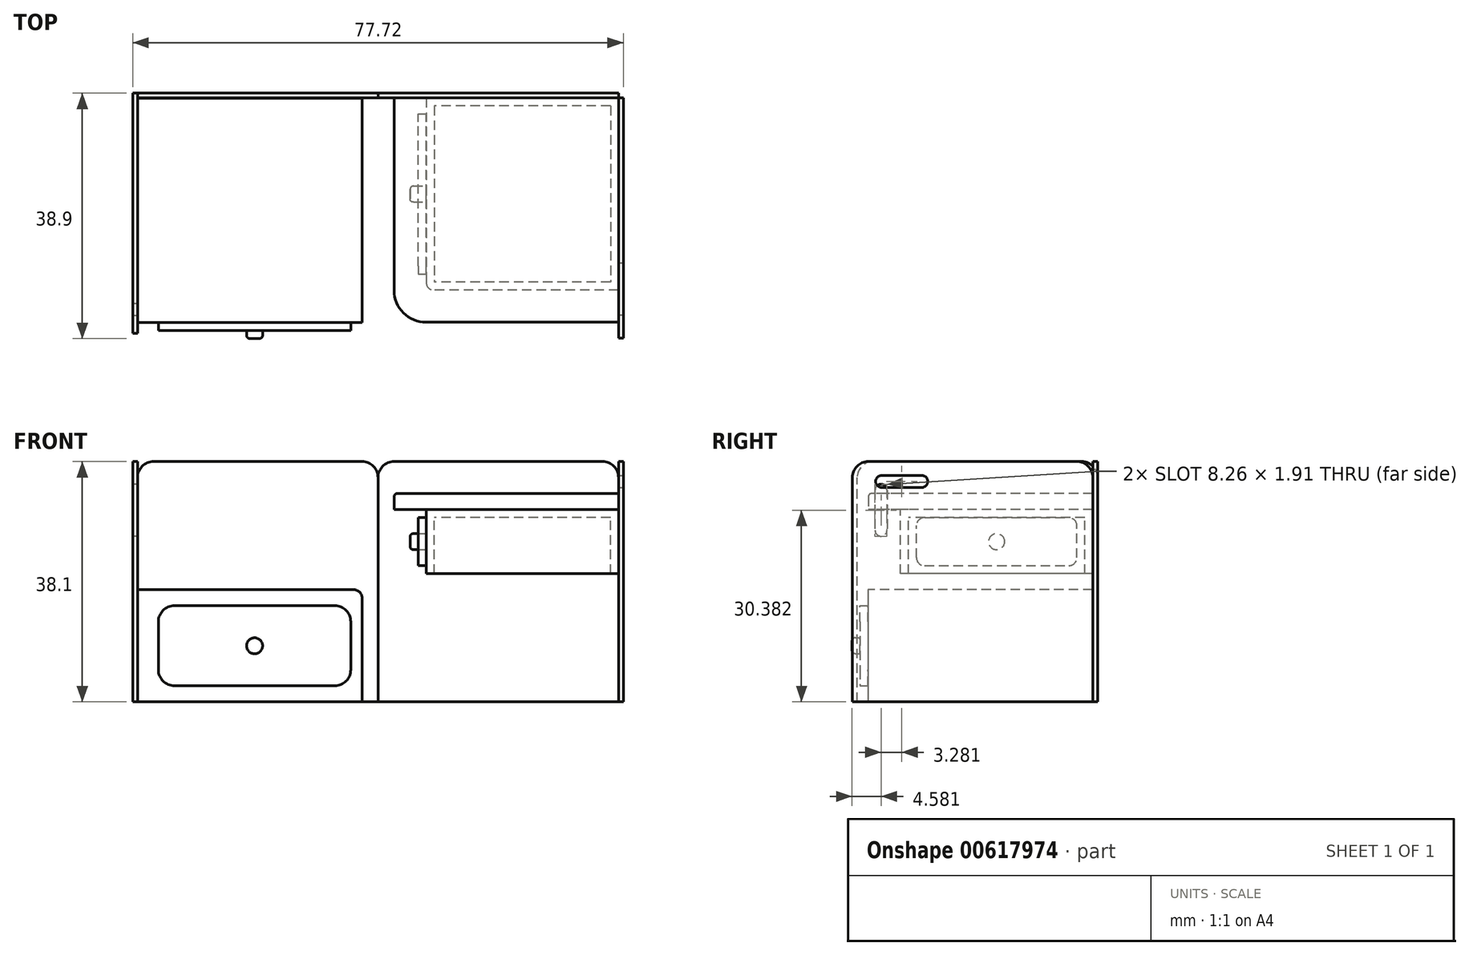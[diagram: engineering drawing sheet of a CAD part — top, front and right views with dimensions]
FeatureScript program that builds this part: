
annotation { "Feature Type Name" : "Feature", "Feature Type Description" : "" }
export const myFeature = defineFeature(function(context is Context, id is Id, definition is map)
    precondition{}
    {
        {
            var Q0;
            Q0=qCreatedBy(makeId("Right.planeOp"),FACE);
            var sketch = newSketch(context, id + "F0", { "sketchPlane" : qUnion([Q0])});
            skLineSegment(sketch, "E0.bottom", {"start": v(0, 0) * mm, "end": v(-38.1, 0) * mm});
            skLineSegment(sketch, "E0.top", {"start": v(0, 38.1) * mm, "end": v(-38.1, 38.1) * mm});
            skLineSegment(sketch, "E0.left", {"start": v(0, 0) * mm, "end": v(0, 38.1) * mm});
            skLineSegment(sketch, "E0.right", {"start": v(-38.1, 0) * mm, "end": v(-38.1, 38.1) * mm});
            skSolve(sketch);
        }
        {
            var Q0;
            Q0=qCreatedBy(makeId("Front.planeOp"),FACE);
            var sketch = newSketch(context, id + "F1", { "sketchPlane" : qUnion([Q0])});
            skLineSegment(sketch, "E1.0", {"start": v(0, 0) * mm, "end": v(0, 38.1) * mm});
            skLineSegment(sketch, "E2.bottom", {"start": v(0, 38.1) * mm, "end": v(38.1, 38.1) * mm});
            skLineSegment(sketch, "E2.top", {"start": v(0, 0) * mm, "end": v(38.1, 0) * mm});
            skLineSegment(sketch, "E2.left", {"start": v(0, 38.1) * mm, "end": v(0, 0) * mm});
            skLineSegment(sketch, "E2.right", {"start": v(38.1, 38.1) * mm, "end": v(38.1, 0) * mm});
            skLineSegment(sketch, "E3.bottom", {"start": v(38.1, 38.1) * mm, "end": v(76.2, 38.1) * mm});
            skLineSegment(sketch, "E3.top", {"start": v(38.1, 0) * mm, "end": v(76.2, 0) * mm});
            skLineSegment(sketch, "E3.right", {"start": v(76.2, 38.1) * mm, "end": v(76.2, 0) * mm});
            skSolve(sketch);
        }
        {
            var Q0;
            Q0=makeQuery(id+"F0.imprint","IMPRINT",FACE,{"disambiguationData":[TD([[makeQuery(id+"F0.imprint","IMPRINT",EDGE,{"derivedFrom":sQuery(id+"F0.wireOp",EDGE,"E0.bottom")}),-1.0]])]});
            extrude(context, id + "F2", {"entities" : qUnion([Q0]), "oppositeDirection" : true, "depth" : 0.76 * mm, "offsetDistance" : 25.4 * mm});
        }
        {
            var Q0;
            Q0=makeQuery(id+"F1.imprint","IMPRINT",FACE,{"disambiguationData":[TD([[makeQuery(id+"F1.imprint","IMPRINT",EDGE,{"derivedFrom":sQuery(id+"F1.wireOp",EDGE,"E2.bottom")}),-1.0]])]});
            extrude(context, id + "F3", {"entities" : qUnion([Q0]), "depth" : 0.76 * mm, "offsetDistance" : 25.4 * mm});
        }
        {
            var Q0;
            Q0=qCreatedBy(makeId("Top.planeOp"),FACE);
            var sketch = newSketch(context, id + "F4", { "sketchPlane" : qUnion([Q0])});
            skPoint(sketch, "E4.0", {"position": v(0, -0.8) * mm});
            skLineSegment(sketch, "E5.bottom", {"start": v(0, -0.8) * mm, "end": v(35.56, -0.8) * mm});
            skLineSegment(sketch, "E5.top", {"start": v(0, -36.36) * mm, "end": v(35.56, -36.36) * mm});
            skLineSegment(sketch, "E5.left", {"start": v(0, -0.8) * mm, "end": v(0, -36.36) * mm});
            skLineSegment(sketch, "E5.right", {"start": v(35.56, -0.8) * mm, "end": v(35.56, -36.36) * mm});
            skSolve(sketch);
        }
        {
            var Q0;
            Q0=makeQuery(id+"F4.imprint","IMPRINT",FACE,{"disambiguationData":[TD([[makeQuery(id+"F4.imprint","IMPRINT",EDGE,{"derivedFrom":sQuery(id+"F4.wireOp",EDGE,"E5.bottom")}),-1.0]])]});
            extrude(context, id + "F5", {"entities" : qUnion([Q0]), "depth" : 17.78 * mm});
        }
        {
            var Q0;
            Q0=makeQuery(id+"F5.opExtrude","CAP_FACE",FACE,{"disambiguationData":[OSD([sQuery(id+"F4.wireOp",EDGE,"E5.bottom"),sQuery(id+"F4.wireOp",EDGE,"E5.top"),sQuery(id+"F4.wireOp",EDGE,"E5.left"),sQuery(id+"F4.wireOp",EDGE,"E5.right")])],"isStart":false});
            cPlane(context, id + "F6", {"entities" : qUnion([Q0]), "cplaneType" : CPlaneType.OFFSET, "offset" : 12.7 * mm, "width" : 152.4 * mm, "height" : 152.4 * mm});
        }
        {
            var Q0;
            Q0=qCreatedBy(id+"F6.planeOp",FACE);
            var sketch = newSketch(context, id + "F7", { "sketchPlane" : qUnion([Q0])});
            skLineSegment(sketch, "E6.bottom", {"start": v(76.2, -0.76) * mm, "end": v(40.64, -0.76) * mm});
            skLineSegment(sketch, "E6.top", {"start": v(76.2, -36.32) * mm, "end": v(40.64, -36.32) * mm});
            skLineSegment(sketch, "E6.left", {"start": v(76.2, -0.76) * mm, "end": v(76.2, -36.32) * mm});
            skLineSegment(sketch, "E6.right", {"start": v(40.64, -0.76) * mm, "end": v(40.64, -36.32) * mm});
            skSolve(sketch);
        }
        {
            var Q0;
            Q0=qCreatedBy(id+"F6.planeOp",FACE);
            var sketch = newSketch(context, id + "F8", { "sketchPlane" : qUnion([Q0])});
            skLineSegment(sketch, "E7.bottom", {"start": v(76.2, -0.76) * mm, "end": v(45.72, -0.76) * mm});
            skLineSegment(sketch, "E7.top", {"start": v(76.2, -31.24) * mm, "end": v(45.72, -31.24) * mm});
            skLineSegment(sketch, "E7.left", {"start": v(76.2, -0.76) * mm, "end": v(76.2, -31.24) * mm});
            skLineSegment(sketch, "E7.right", {"start": v(45.72, -0.76) * mm, "end": v(45.72, -31.24) * mm});
            skSolve(sketch);
        }
        {
            var Q0;
            Q0=makeQuery(id+"F8.imprint","IMPRINT",FACE,{"disambiguationData":[TD([[makeQuery(id+"F8.imprint","IMPRINT",EDGE,{"derivedFrom":sQuery(id+"F8.wireOp",EDGE,"E7.bottom")}),1.0]])]});
            extrude(context, id + "F9", {"entities" : qUnion([Q0]), "oppositeDirection" : true, "depth" : 10.16 * mm});
        }
        {
            var Q0;
            Q0=qSketchRegion(id+"F7",true);
            extrude(context, id + "F10", {"entities" : qUnion([Q0]), "depth" : 2.54 * mm});
        }
        {
            var Q0;
            Q0=makeQuery(id+"F5.opExtrude","SWEPT_FACE",FACE,{"disambiguationData":[OSD([sQuery(id+"F4.wireOp",EDGE,"E5.top")])]});
            var sketch = newSketch(context, id + "F11", { "sketchPlane" : qUnion([Q0])});
            skLineSegment(sketch, "E8.0", {"start": v(35.56, 17.78) * mm, "end": v(35.56, 0) * mm});
            skLineSegment(sketch, "E9.0.2", {"start": v(35.56, 17.78) * mm, "end": v(0, 17.78) * mm});
            skLineSegment(sketch, "E9.0.3", {"start": v(0, 17.78) * mm, "end": v(0, 0) * mm});
            skLineSegment(sketch, "E10.bottom", {"start": v(33.78, 15.24) * mm, "end": v(3.3, 15.24) * mm});
            skLineSegment(sketch, "E10.top", {"start": v(33.78, 2.54) * mm, "end": v(3.3, 2.54) * mm});
            skLineSegment(sketch, "E10.left", {"start": v(33.78, 15.24) * mm, "end": v(33.78, 2.54) * mm});
            skLineSegment(sketch, "E10.right", {"start": v(3.3, 15.24) * mm, "end": v(3.3, 2.54) * mm});
            skPoint(sketch, "E10.middle", {"position": v(18.54, 8.9) * mm});
            skSolve(sketch);
        }
        {
            var Q0;
            Q0=makeQuery(id+"F11.imprint","IMPRINT",FACE,{"disambiguationData":[TD([[makeQuery(id+"F11.imprint","IMPRINT",EDGE,{"derivedFrom":sQuery(id+"F11.wireOp",EDGE,"E10.bottom")}),1.0]])]});
            extrude(context, id + "F12", {"entities" : qUnion([Q0]), "depth" : 1.27 * mm});
        }
        {
            var Q0;
            Q0=makeQuery(id+"F12.opExtrude","CAP_FACE",FACE,{"disambiguationData":[OSD([sQuery(id+"F11.wireOp",EDGE,"E10.bottom"),sQuery(id+"F11.wireOp",EDGE,"E10.top"),sQuery(id+"F11.wireOp",EDGE,"E10.left"),sQuery(id+"F11.wireOp",EDGE,"E10.right")])],"isStart":false});
            var sketch = newSketch(context, id + "F13", { "sketchPlane" : qUnion([Q0])});
            skCircle(sketch, "E11", {"center": v(18.54, 8.89) * mm, "radius": 1.27 * mm});
            skSolve(sketch);
        }
        {
            var Q0;
            Q0=makeQuery(id+"F13.imprint","IMPRINT",FACE,{"disambiguationData":[TD([[makeQuery(id+"F13.imprint","IMPRINT",EDGE,{"derivedFrom":sQuery(id+"F13.wireOp",EDGE,"E11")}),1.0]])]});
            extrude(context, id + "F14", {"entities" : qUnion([Q0]), "depth" : 1.27 * mm});
        }
        {
            var Q0;
            Q0=makeQuery(id+"F9.opExtrude","SWEPT_FACE",FACE,{"disambiguationData":[OSD([sQuery(id+"F8.wireOp",EDGE,"E7.right")])]});
            var sketch = newSketch(context, id + "F15", { "sketchPlane" : qUnion([Q0])});
            skLineSegment(sketch, "E12.bottom", {"start": v(28.7, 21.59) * mm, "end": v(3.3, 21.59) * mm});
            skLineSegment(sketch, "E12.top", {"start": v(28.7, 29.2) * mm, "end": v(3.3, 29.2) * mm});
            skLineSegment(sketch, "E12.left", {"start": v(28.7, 21.59) * mm, "end": v(28.7, 29.2) * mm});
            skLineSegment(sketch, "E12.right", {"start": v(3.3, 21.59) * mm, "end": v(3.3, 29.2) * mm});
            skPoint(sketch, "E12.middle", {"position": v(16, 25.4) * mm});
            skSolve(sketch);
        }
        {
            var Q0;
            Q0=makeQuery(id+"F15.imprint","IMPRINT",FACE,{"disambiguationData":[TD([[makeQuery(id+"F15.imprint","IMPRINT",EDGE,{"derivedFrom":sQuery(id+"F15.wireOp",EDGE,"E12.bottom")}),1.0]])]});
            var sketch = newSketch(context, id + "F16", { "sketchPlane" : qUnion([Q0])});
            skCircle(sketch, "E13", {"center": v(16, 25.4) * mm, "radius": 1.27 * mm});
            skSolve(sketch);
        }
        {
            var Q0;
            Q0=makeQuery(id+"F16.imprint","IMPRINT",FACE,{"disambiguationData":[TD([[makeQuery(id+"F16.imprint","IMPRINT",EDGE,{"derivedFrom":sQuery(id+"F16.wireOp",EDGE,"E13")}),1.0]])]});
            extrude(context, id + "F17", {"entities" : qUnion([Q0]), "depth" : 2.54 * mm});
        }
        {
            var Q0;
            Q0=makeQuery(id+"F15.imprint","IMPRINT",FACE,{"disambiguationData":[TD([[makeQuery(id+"F15.imprint","IMPRINT",EDGE,{"derivedFrom":sQuery(id+"F15.wireOp",EDGE,"E12.bottom")}),-1.0]])]});
            extrude(context, id + "F18", {"entities" : qUnion([Q0]), "depth" : 1.27 * mm});
        }
        {
            var Q0;
            Q0=makeQuery(id+"F2.opExtrude","SWEPT_EDGE",EDGE,{"disambiguationData":[OSD([sQuery(id+"F0.wireOp",EDGE,"E0.top"),sQuery(id+"F0.wireOp",EDGE,"E0.right")])]});
            var Q1;
            Q1=makeQuery(id+"F2.opExtrude","SWEPT_EDGE",EDGE,{"disambiguationData":[OSD([sQuery(id+"F0.wireOp",EDGE,"E0.top"),sQuery(id+"F0.wireOp",EDGE,"E0.left")])]});
            var Q2;
            Q2=makeQuery(id+"F3.opExtrude","SWEPT_EDGE",EDGE,{"disambiguationData":[OSD([sQuery(id+"FI0QwBpxzJms6q6_1.wireOp",EDGE,"EPlBsMqQ-QzQ8-VdCQ-xvKd-hzmvY7jMW2L1.bottom"),sQuery(id+"FI0QwBpxzJms6q6_1.wireOp",EDGE,"EPlBsMqQ-QzQ8-VdCQ-xvKd-hzmvY7jMW2L1.right")])]});
            var Q3;
            Q3=makeQuery(id+"FcK2yJQiMoCniT7_2.opExtrude","SWEPT_EDGE",EDGE,{"disambiguationData":[OSD([sQuery(id+"FKOlXeHhfTV6Gp4_1.wireOp",EDGE,"gBm9quYi-xdeT-jJYe-hTa2-NPwO5Kq9pGmv.bottom"),sQuery(id+"FKOlXeHhfTV6Gp4_1.wireOp",EDGE,"gBm9quYi-xdeT-jJYe-hTa2-NPwO5Kq9pGmv.right")])]});
            var Q4;
            Q4=makeQuery(id+"FcK2yJQiMoCniT7_2.opExtrude","SWEPT_EDGE",EDGE,{"disambiguationData":[OSD([sQuery(id+"FKOlXeHhfTV6Gp4_1.wireOp",EDGE,"gBm9quYi-xdeT-jJYe-hTa2-NPwO5Kq9pGmv.bottom"),sQuery(id+"FKOlXeHhfTV6Gp4_1.wireOp",EDGE,"gBm9quYi-xdeT-jJYe-hTa2-NPwO5Kq9pGmv.left")])]});
            var Q5;
            Q5=makeQuery(id+"F3.opExtrude","SWEPT_EDGE",EDGE,{"disambiguationData":[OSD([sQuery(id+"F1.wireOp",EDGE,"E3.bottom"),sQuery(id+"F1.wireOp",EDGE,"E3.right")])]});
            var Q6;
            Q6=makeQuery(id+"F3.opExtrude","SWEPT_EDGE",EDGE,{"disambiguationData":[OSD([sQuery(id+"F1.wireOp",EDGE,"E2.bottom"),sQuery(id+"F1.wireOp",EDGE,"E2.left")])]});
            fillet(context, id + "F19", {"entities" : qUnion([Q0, Q1, Q2, Q3, Q4, Q5, Q6]), "radius" : 2.54 * mm, "tangentPropagation" : true, "allowEdgeOverflow" : false});
        }
        {
            var Q0;
            Q0=makeQuery(id+"F10.opExtrude","SWEPT_EDGE",EDGE,{"disambiguationData":[OSD([sQuery(id+"F7.wireOp",EDGE,"E6.top"),sQuery(id+"F7.wireOp",EDGE,"E6.right")])]});
            fillet(context, id + "F20", {"entities" : qUnion([Q0]), "radius" : 5.08 * mm, "tangentPropagation" : true, "allowEdgeOverflow" : false});
        }
        {
            var Q0;
            Q0=makeQuery(id+"F9.opExtrude","SWEPT_EDGE",EDGE,{"disambiguationData":[OSD([sQuery(id+"F8.wireOp",EDGE,"E7.top"),sQuery(id+"F8.wireOp",EDGE,"E7.right")])]});
            var Q1;
            Q1=makeQuery(id+"F5.opExtrude","CAP_EDGE",EDGE,{"disambiguationData":[OSD([sQuery(id+"F4.wireOp",EDGE,"E5.right")])],"isStart":false});
            fillet(context, id + "F21", {"entities" : qUnion([Q0, Q1]), "radius" : 1.27 * mm, "tangentPropagation" : true, "allowEdgeOverflow" : false});
        }
        {
            var Q0;
            Q0=makeQuery(id+"F2.opExtrude","CAP_FACE",FACE,{"disambiguationData":[OSD([sQuery(id+"F0.wireOp",EDGE,"E0.bottom"),sQuery(id+"F0.wireOp",EDGE,"E0.top"),sQuery(id+"F0.wireOp",EDGE,"E0.left"),sQuery(id+"F0.wireOp",EDGE,"E0.right")])],"isStart":true});
            var sketch = newSketch(context, id + "F22", { "sketchPlane" : qUnion([Q0])});
            skLineSegment(sketch, "E14.left", {"start": v(33.38, 34.48) * mm, "end": v(33.38, 28.13) * mm});
            skLineSegment(sketch, "E14.right", {"start": v(35.28, 34.48) * mm, "end": v(35.28, 28.13) * mm});
            skArc(sketch, "E15", {"start": v(35.28, 34.48) * mm, "mid": v(34.33, 35.43) * mm, "end": v(33.38, 34.48) * mm});
            skArc(sketch, "E16", {"start": v(33.38, 28.13) * mm, "mid": v(34.33, 27.18) * mm, "end": v(35.28, 28.13) * mm});
            skSolve(sketch);
        }
        {
            var Q0;
            Q0=qSketchRegion(id+"F22",true);
            extrude(context, id + "F23", {"entities" : qUnion([Q0]), "operationType" : NewBodyOperationType.REMOVE, "oppositeDirection" : true, "depth" : 12.7 * mm, "offsetDistance" : 25.4 * mm});
        }
        {
            var Q0;
            Q0=makeQuery(id+"F1.imprint","IMPRINT",FACE,{"disambiguationData":[TD([[makeQuery(id+"F1.imprint","IMPRINT",EDGE,{"derivedFrom":sQuery(id+"F1.wireOp",EDGE,"E3.bottom")}),-1.0]])]});
            extrude(context, id + "F24", {"entities" : qUnion([Q0]), "depth" : 0.76 * mm, "offsetDistance" : 25.4 * mm});
        }
        {
            var Q0;
            Q0=qCreatedBy(makeId("Right.planeOp"),FACE);
            cPlane(context, id + "F25", {"entities" : qUnion([Q0]), "cplaneType" : CPlaneType.OFFSET, "offset" : 76.2 * mm, "width" : 152.4 * mm, "height" : 152.4 * mm});
        }
        {
            var Q0;
            Q0=qCreatedBy(id+"F25.planeOp",FACE);
            var sketch = newSketch(context, id + "F26", { "sketchPlane" : qUnion([Q0])});
            skLineSegment(sketch, "E17.bottom", {"start": v(-0.76, 38.1) * mm, "end": v(-38.86, 38.1) * mm});
            skLineSegment(sketch, "E17.top", {"start": v(-0.76, 0) * mm, "end": v(-38.86, 0) * mm});
            skLineSegment(sketch, "E17.left", {"start": v(-0.76, 38.1) * mm, "end": v(-0.76, 0) * mm});
            skLineSegment(sketch, "E17.right", {"start": v(-38.86, 38.1) * mm, "end": v(-38.86, 0) * mm});
            skSolve(sketch);
        }
        {
            var Q0;
            Q0=qSketchRegion(id+"F26",true);
            extrude(context, id + "F27", {"entities" : qUnion([Q0]), "depth" : 0.76 * mm, "offsetDistance" : 25.4 * mm});
        }
        {
            var Q0;
            Q0=makeQuery(id+"F27.opExtrude","CAP_FACE",FACE,{"disambiguationData":[OSD([sQuery(id+"F26.wireOp",EDGE,"E17.bottom"),sQuery(id+"F26.wireOp",EDGE,"E17.top"),sQuery(id+"F26.wireOp",EDGE,"E17.left"),sQuery(id+"F26.wireOp",EDGE,"E17.right")])],"isStart":false});
            var sketch = newSketch(context, id + "F28", { "sketchPlane" : qUnion([Q0])});
            skLineSegment(sketch, "E18.bottom", {"start": v(-34.21, 35.9) * mm, "end": v(-27.86, 35.9) * mm});
            skLineSegment(sketch, "E18.top", {"start": v(-34.21, 33.99) * mm, "end": v(-27.86, 33.99) * mm});
            skArc(sketch, "E19", {"start": v(-27.86, 33.99) * mm, "mid": v(-26.91, 34.94) * mm, "end": v(-27.86, 35.9) * mm});
            skArc(sketch, "E20", {"start": v(-34.21, 35.9) * mm, "mid": v(-35.17, 34.94) * mm, "end": v(-34.21, 33.99) * mm});
            skSolve(sketch);
        }
        {
            var Q0;
            Q0=makeQuery(id+"F28.imprint","IMPRINT",FACE,{"disambiguationData":[TD([[makeQuery(id+"F28.imprint","IMPRINT",EDGE,{"derivedFrom":sQuery(id+"F28.wireOp",EDGE,"E18.bottom")}),-1.0]])]});
            extrude(context, id + "F29", {"entities" : qUnion([Q0]), "operationType" : NewBodyOperationType.REMOVE, "oppositeDirection" : true, "depth" : 12.7 * mm, "offsetDistance" : 25.4 * mm});
        }
        {
            var Q0;
            Q0=makeQuery(id+"F24.opExtrude","SWEPT_EDGE",EDGE,{"disambiguationData":[OSD([sQuery(id+"F1.wireOp",EDGE,"E3.bottom"),sQuery(id+"F1.wireOp",EDGE,"E3.right")])]});
            var Q1;
            Q1=makeQuery(id+"F27.opExtrude","SWEPT_EDGE",EDGE,{"disambiguationData":[OSD([sQuery(id+"F26.wireOp",EDGE,"E17.bottom"),sQuery(id+"F26.wireOp",EDGE,"E17.left")])]});
            var Q2;
            Q2=makeQuery(id+"F24.opExtrude","SWEPT_EDGE",EDGE,{"disambiguationData":[OSD([sQuery(id+"F1.wireOp",EDGE,"E2.bottom"),sQuery(id+"F1.wireOp",EDGE,"E3.bottom"),sQuery(id+"F1.wireOp",EDGE,"E2.right")])]});
            var Q3;
            Q3=makeQuery(id+"F27.opExtrude","SWEPT_EDGE",EDGE,{"disambiguationData":[OSD([sQuery(id+"F26.wireOp",EDGE,"E17.bottom"),sQuery(id+"F26.wireOp",EDGE,"E17.right")])]});
            fillet(context, id + "F30", {"entities" : qUnion([Q0, Q1, Q2, Q3]), "radius" : 2.54 * mm, "tangentPropagation" : true, "allowEdgeOverflow" : false});
        }
        {
            var Q0;
            Q0=makeQuery(id+"F9.opExtrude","CAP_FACE",FACE,{"disambiguationData":[OSD([sQuery(id+"F8.wireOp",EDGE,"E7.bottom"),sQuery(id+"F8.wireOp",EDGE,"E7.top"),sQuery(id+"F8.wireOp",EDGE,"E7.left"),sQuery(id+"F8.wireOp",EDGE,"E7.right")])],"isStart":false});
            shell(context, id + "F31", {"entities" : qUnion([Q0]), "thickness" : 1.27 * mm});
        }
        {
            var Q0;
            Q0=makeQuery(id+"F2.opExtrude","CAP_FACE",FACE,{"disambiguationData":[OSD([sQuery(id+"F0.wireOp",EDGE,"E0.bottom"),sQuery(id+"F0.wireOp",EDGE,"E0.top"),sQuery(id+"F0.wireOp",EDGE,"E0.left"),sQuery(id+"F0.wireOp",EDGE,"E0.right")])],"isStart":false});
            var sketch = newSketch(context, id + "F32", { "sketchPlane" : qUnion([Q0])});
            skLineSegment(sketch, "E21.left", {"start": v(33.37, 33.56) * mm, "end": v(33.37, 27.2) * mm});
            skLineSegment(sketch, "E21.right", {"start": v(35.27, 33.56) * mm, "end": v(35.27, 27.2) * mm});
            skArc(sketch, "E22", {"start": v(35.27, 33.56) * mm, "mid": v(34.32, 34.5) * mm, "end": v(33.37, 33.56) * mm});
            skArc(sketch, "E23", {"start": v(33.37, 27.2) * mm, "mid": v(34.32, 26.25) * mm, "end": v(35.27, 27.2) * mm});
            skSolve(sketch);
        }
        {
            var Q0;
            Q0 = qSketchRegion(id + "F32", true);
            extrude(context, id + "F33", {"entities" : qUnion([Q0]), "operationType" : NewBodyOperationType.REMOVE, "oppositeDirection" : true, "depth" : 25.4 * mm, "offsetDistance" : 25.4 * mm});
        }
        {
            var Q0;
            Q0=makeQuery(id+"F10.opExtrude","CAP_EDGE",EDGE,{"disambiguationData":[OSD([sQuery(id+"F7.wireOp",EDGE,"E6.right")])],"isStart":false});
            fillet(context, id + "F34", {"entities" : qUnion([Q0]), "radius" : 0.5 * mm, "tangentPropagation" : true, "allowEdgeOverflow" : false});
        }
        {
            var Q0;
            Q0=makeQuery(id+"F14.opExtrude","CAP_FACE",FACE,{"disambiguationData":[OSD([sQuery(id+"F13.wireOp",EDGE,"E11")])],"isStart":false});
            fillet(context, id + "F35", {"entities" : qUnion([Q0]), "radius" : 0.5 * mm, "tangentPropagation" : true, "allowEdgeOverflow" : false});
        }
        {
            var Q0;
            Q0=makeQuery(id+"F17.opExtrude","CAP_EDGE",EDGE,{"disambiguationData":[OSD([sQuery(id+"F16.wireOp",EDGE,"E13")])],"isStart":false});
            fillet(context, id + "F36", {"entities" : qUnion([Q0]), "radius" : 0.5 * mm, "tangentPropagation" : true, "allowEdgeOverflow" : false});
        }
        {
            var Q0;
            Q0=makeQuery(id+"F12.opExtrude","SWEPT_EDGE",EDGE,{"disambiguationData":[OSD([sQuery(id+"F11.wireOp",EDGE,"E10.bottom"),sQuery(id+"F11.wireOp",EDGE,"E10.right")])]});
            var Q1;
            Q1=makeQuery(id+"F12.opExtrude","SWEPT_EDGE",EDGE,{"disambiguationData":[OSD([sQuery(id+"F11.wireOp",EDGE,"E10.top"),sQuery(id+"F11.wireOp",EDGE,"E10.right")])]});
            var Q2;
            Q2=makeQuery(id+"F12.opExtrude","SWEPT_EDGE",EDGE,{"disambiguationData":[OSD([sQuery(id+"F11.wireOp",EDGE,"E10.top"),sQuery(id+"F11.wireOp",EDGE,"E10.left")])]});
            var Q3;
            Q3=makeQuery(id+"F12.opExtrude","SWEPT_EDGE",EDGE,{"disambiguationData":[OSD([sQuery(id+"F11.wireOp",EDGE,"E10.bottom"),sQuery(id+"F11.wireOp",EDGE,"E10.left")])]});
            fillet(context, id + "F37", {"entities" : qUnion([Q0, Q1, Q2, Q3]), "radius" : 2.54 * mm, "tangentPropagation" : true, "allowEdgeOverflow" : false});
        }
        {
            var Q0;
            Q0=makeQuery(id+"F18.opExtrude","SWEPT_EDGE",EDGE,{"disambiguationData":[OSD([sQuery(id+"F15.wireOp",EDGE,"E12.bottom"),sQuery(id+"F15.wireOp",EDGE,"E12.left")])]});
            var Q1;
            Q1=makeQuery(id+"F18.opExtrude","SWEPT_EDGE",EDGE,{"disambiguationData":[OSD([sQuery(id+"F15.wireOp",EDGE,"E12.top"),sQuery(id+"F15.wireOp",EDGE,"E12.left")])]});
            var Q2;
            Q2=makeQuery(id+"F18.opExtrude","SWEPT_EDGE",EDGE,{"disambiguationData":[OSD([sQuery(id+"F15.wireOp",EDGE,"E12.bottom"),sQuery(id+"F15.wireOp",EDGE,"E12.right")])]});
            var Q3;
            Q3=makeQuery(id+"F18.opExtrude","SWEPT_EDGE",EDGE,{"disambiguationData":[OSD([sQuery(id+"F15.wireOp",EDGE,"E12.top"),sQuery(id+"F15.wireOp",EDGE,"E12.right")])]});
            fillet(context, id + "F38", {"entities" : qUnion([Q0, Q1, Q2, Q3]), "radius" : 1.27 * mm, "tangentPropagation" : true, "allowEdgeOverflow" : false});
        }
    });
